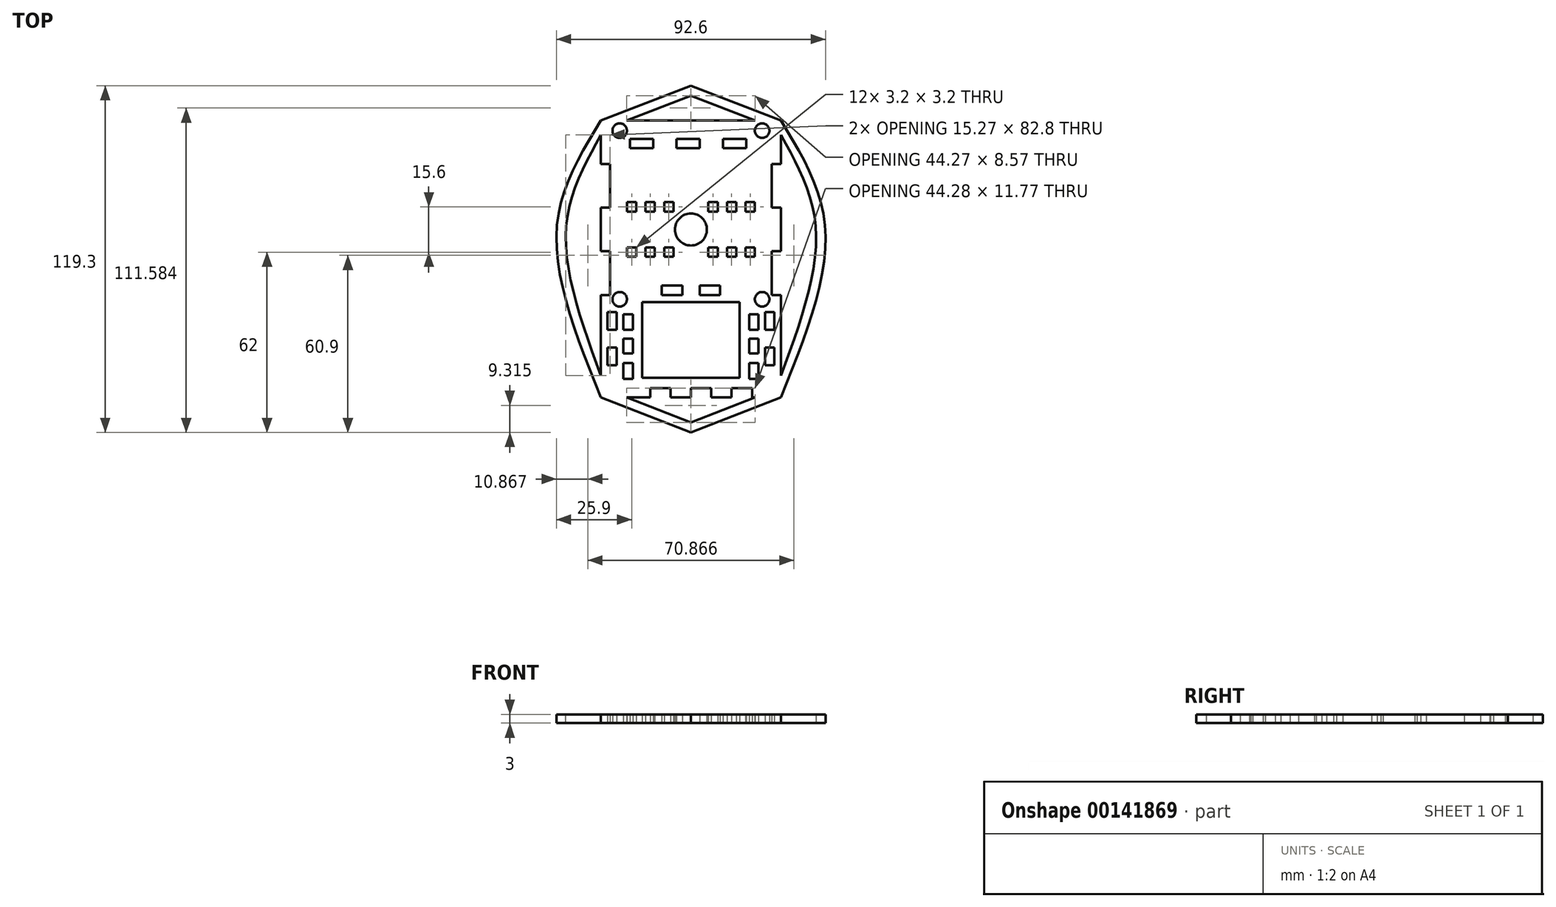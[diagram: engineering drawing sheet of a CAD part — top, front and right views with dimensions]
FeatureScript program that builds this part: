
annotation { "Feature Type Name" : "Feature", "Feature Type Description" : "" }
export const myFeature = defineFeature(function(context is Context, id is Id, definition is map)
    precondition{}
    {
        {
            var Q0;
            Q0=qCreatedBy(makeId("Top.planeOp"),FACE);
            var sketch = newSketch(context, id + "F0", { "sketchPlane" : qUnion([Q0])});
            skLineSegment(sketch, "E0.top", {"start": v(0, 37.5) * mm, "end": v(-22.14, 37.5) * mm});
            skLineSegment(sketch, "E0.right", {"start": v(-31, -32.5) * mm, "end": v(-31, -22.5) * mm});
            skPoint(sketch, "E0.middle", {"position": v(0, 0) * mm});
            skLineSegment(sketch, "E1", {"start": v(-31, 22.5) * mm, "end": v(-27.8, 22.5) * mm});
            skLineSegment(sketch, "E2", {"start": v(-27.8, 22.5) * mm, "end": v(-27.8, 7.5) * mm});
            skLineSegment(sketch, "E3", {"start": v(-27.8, 7.5) * mm, "end": v(-31, 7.5) * mm});
            skLineSegment(sketch, "E4", {"start": v(-31, 7.5) * mm, "end": v(-31, -7.5) * mm});
            skLineSegment(sketch, "E5", {"start": v(-31, -7.5) * mm, "end": v(-27.8, -7.5) * mm});
            skLineSegment(sketch, "E6", {"start": v(-27.8, -7.5) * mm, "end": v(-27.8, -22.5) * mm});
            skLineSegment(sketch, "E7", {"start": v(-27.8, -22.5) * mm, "end": v(-31, -22.5) * mm});
            skLineSegment(sketch, "E8", {"start": v(-31, -22.5) * mm, "end": v(-31, -32.5) * mm});
            skLineSegment(sketch, "E9", {"start": v(27.8, 22.5) * mm, "end": v(31, 22.5) * mm});
            skLineSegment(sketch, "E10", {"start": v(31, 7.5) * mm, "end": v(27.8, 7.5) * mm});
            skLineSegment(sketch, "E11", {"start": v(27.8, -7.5) * mm, "end": v(31, -7.5) * mm});
            skLineSegment(sketch, "E12", {"start": v(31, -22.5) * mm, "end": v(27.8, -22.5) * mm});
            skLineSegment(sketch, "E13.trimOffspring", {"start": v(-31, 22.5) * mm, "end": v(-31, 32.5) * mm});
            skLineSegment(sketch, "E14.trimOffspring", {"start": v(-31, -7.5) * mm, "end": v(-31, 7.5) * mm});
            skCircle(sketch, "E15", {"center": v(0, 0) * mm, "radius": 5.5 * mm});
            skLineSegment(sketch, "E16", {"start": v(0, 0) * mm, "end": v(5.5, 0) * mm, "construction": true});
            skLineSegment(sketch, "E17", {"start": v(-31, 0) * mm, "end": v(0, 0) * mm, "construction": true});
            skLineSegment(sketch, "E18", {"start": v(5.5, 0) * mm, "end": v(6, 0) * mm, "construction": true});
            skLineSegment(sketch, "E19", {"start": v(6, 0) * mm, "end": v(6, 9.4) * mm, "construction": true});
            skLineSegment(sketch, "E20.bottom", {"start": v(6, 9.4) * mm, "end": v(9.2, 9.4) * mm});
            skLineSegment(sketch, "E20.top", {"start": v(6, 6.2) * mm, "end": v(9.2, 6.2) * mm});
            skLineSegment(sketch, "E20.left", {"start": v(6, 9.4) * mm, "end": v(6, 6.2) * mm});
            skLineSegment(sketch, "E20.right", {"start": v(9.2, 9.4) * mm, "end": v(9.2, 6.2) * mm});
            skLineSegment(sketch, "E21", {"start": v(6, 0) * mm, "end": v(12.4, 0) * mm, "construction": true});
            skLineSegment(sketch, "E22", {"start": v(12.4, 0) * mm, "end": v(12.4, 9.4) * mm, "construction": true});
            skLineSegment(sketch, "E23", {"start": v(12.4, 0) * mm, "end": v(18.8, 0) * mm, "construction": true});
            skLineSegment(sketch, "E24", {"start": v(18.8, 0) * mm, "end": v(18.8, 9.4) * mm, "construction": true});
            skLineSegment(sketch, "E25", {"start": v(18.8, 0) * mm, "end": v(24, 0) * mm, "construction": true});
            skLineSegment(sketch, "E26.bottom", {"start": v(12.4, 9.4) * mm, "end": v(15.6, 9.4) * mm});
            skLineSegment(sketch, "E26.top", {"start": v(12.4, 6.2) * mm, "end": v(15.6, 6.2) * mm});
            skLineSegment(sketch, "E26.left", {"start": v(12.4, 9.4) * mm, "end": v(12.4, 6.2) * mm});
            skLineSegment(sketch, "E26.right", {"start": v(15.6, 9.4) * mm, "end": v(15.6, 6.2) * mm});
            skLineSegment(sketch, "E27.bottom", {"start": v(18.8, 9.4) * mm, "end": v(22, 9.4) * mm});
            skLineSegment(sketch, "E27.top", {"start": v(18.8, 6.2) * mm, "end": v(22, 6.2) * mm});
            skLineSegment(sketch, "E27.left", {"start": v(18.8, 9.4) * mm, "end": v(18.8, 6.2) * mm});
            skLineSegment(sketch, "E27.right", {"start": v(22, 9.4) * mm, "end": v(22, 6.2) * mm});
            skLineSegment(sketch, "E28.MirrorCS", {"start": v(-5.5, 0) * mm, "end": v(-6, 0) * mm, "construction": true});
            skLineSegment(sketch, "E29.MirrorCS", {"start": v(-6, 0) * mm, "end": v(-12.4, 0) * mm, "construction": true});
            skLineSegment(sketch, "E30.MirrorCS", {"start": v(-18.8, 0) * mm, "end": v(-24, 0) * mm, "construction": true});
            skLineSegment(sketch, "E31.MirrorCS", {"start": v(-12.4, 0) * mm, "end": v(-18.8, 0) * mm, "construction": true});
            skLineSegment(sketch, "E32", {"start": v(-31, 0) * mm, "end": v(27.8, 0) * mm, "construction": true});
            skLineSegment(sketch, "E33.MirrorCS", {"start": v(0, 0) * mm, "end": v(0, 30) * mm, "construction": true});
            skLineSegment(sketch, "E34.MirrorCS", {"start": v(6, -9.4) * mm, "end": v(9.2, -9.4) * mm});
            skLineSegment(sketch, "E35.MirrorCS", {"start": v(12.4, -9.4) * mm, "end": v(12.4, -6.2) * mm});
            skLineSegment(sketch, "E36.MirrorCS", {"start": v(18.8, -9.4) * mm, "end": v(18.8, -6.2) * mm});
            skLineSegment(sketch, "E37.MirrorCS", {"start": v(6, -9.4) * mm, "end": v(6, -6.2) * mm});
            skLineSegment(sketch, "E38.MirrorCS", {"start": v(18.8, -9.4) * mm, "end": v(22, -9.4) * mm});
            skLineSegment(sketch, "E39.MirrorCS", {"start": v(6, -6.2) * mm, "end": v(9.2, -6.2) * mm});
            skLineSegment(sketch, "E40.MirrorCS", {"start": v(12.4, 0) * mm, "end": v(12.4, -9.4) * mm, "construction": true});
            skLineSegment(sketch, "E41.MirrorCS", {"start": v(9.2, -9.4) * mm, "end": v(9.2, -6.2) * mm});
            skLineSegment(sketch, "E42.MirrorCS", {"start": v(15.6, -9.4) * mm, "end": v(15.6, -6.2) * mm});
            skLineSegment(sketch, "E43.MirrorCS", {"start": v(12.4, -6.2) * mm, "end": v(15.6, -6.2) * mm});
            skLineSegment(sketch, "E44.MirrorCS", {"start": v(12.4, -9.4) * mm, "end": v(15.6, -9.4) * mm});
            skLineSegment(sketch, "E45.MirrorCS", {"start": v(18.8, 0) * mm, "end": v(18.8, -9.4) * mm, "construction": true});
            skLineSegment(sketch, "E46.MirrorCS", {"start": v(18.8, -6.2) * mm, "end": v(22, -6.2) * mm});
            skLineSegment(sketch, "E47.MirrorCS", {"start": v(22, -9.4) * mm, "end": v(22, -6.2) * mm});
            skLineSegment(sketch, "E48.MirrorCS", {"start": v(6, 0) * mm, "end": v(6, -9.4) * mm, "construction": true});
            skLineSegment(sketch, "E49.MirrorCS", {"start": v(-9.2, 9.4) * mm, "end": v(-9.2, 6.2) * mm});
            skLineSegment(sketch, "E50.MirrorCS", {"start": v(-15.6, 9.4) * mm, "end": v(-15.6, 6.2) * mm});
            skLineSegment(sketch, "E51.MirrorCS", {"start": v(-12.4, 9.4) * mm, "end": v(-15.6, 9.4) * mm});
            skLineSegment(sketch, "E52.MirrorCS", {"start": v(-18.8, 6.2) * mm, "end": v(-22, 6.2) * mm});
            skLineSegment(sketch, "E53.MirrorCS", {"start": v(-18.8, 9.4) * mm, "end": v(-18.8, 6.2) * mm});
            skLineSegment(sketch, "E54.MirrorCS", {"start": v(-6, 9.4) * mm, "end": v(-9.2, 9.4) * mm});
            skLineSegment(sketch, "E55.MirrorCS", {"start": v(-22, 9.4) * mm, "end": v(-22, 6.2) * mm});
            skLineSegment(sketch, "E56.MirrorCS", {"start": v(-18.8, 9.4) * mm, "end": v(-22, 9.4) * mm});
            skLineSegment(sketch, "E57.MirrorCS", {"start": v(-6, 6.2) * mm, "end": v(-9.2, 6.2) * mm});
            skLineSegment(sketch, "E58.MirrorCS", {"start": v(-12.4, 9.4) * mm, "end": v(-12.4, 6.2) * mm});
            skLineSegment(sketch, "E59.MirrorCS", {"start": v(-12.4, 6.2) * mm, "end": v(-15.6, 6.2) * mm});
            skLineSegment(sketch, "E60.MirrorCS", {"start": v(-6, 9.4) * mm, "end": v(-6, 6.2) * mm});
            skLineSegment(sketch, "E61.MirrorCS", {"start": v(-18.8, -9.4) * mm, "end": v(-18.8, -6.2) * mm});
            skLineSegment(sketch, "E62.MirrorCS", {"start": v(-12.4, -9.4) * mm, "end": v(-12.4, -6.2) * mm});
            skLineSegment(sketch, "E63.MirrorCS", {"start": v(-6, -9.4) * mm, "end": v(-6, -6.2) * mm});
            skLineSegment(sketch, "E64.MirrorCS", {"start": v(-12.4, -9.4) * mm, "end": v(-15.6, -9.4) * mm});
            skLineSegment(sketch, "E65.MirrorCS", {"start": v(-18.8, -6.2) * mm, "end": v(-22, -6.2) * mm});
            skLineSegment(sketch, "E66.MirrorCS", {"start": v(-18.8, -9.4) * mm, "end": v(-22, -9.4) * mm});
            skLineSegment(sketch, "E67.MirrorCS", {"start": v(-12.4, -6.2) * mm, "end": v(-15.6, -6.2) * mm});
            skLineSegment(sketch, "E68.MirrorCS", {"start": v(-12.4, 0) * mm, "end": v(-12.4, -9.4) * mm, "construction": true});
            skLineSegment(sketch, "E69.MirrorCS", {"start": v(-18.8, 0) * mm, "end": v(-18.8, -9.4) * mm, "construction": true});
            skLineSegment(sketch, "E70.MirrorCS", {"start": v(-6, -9.4) * mm, "end": v(-9.2, -9.4) * mm});
            skLineSegment(sketch, "E71.MirrorCS", {"start": v(-6, 0) * mm, "end": v(-6, -9.4) * mm, "construction": true});
            skLineSegment(sketch, "E72.MirrorCS", {"start": v(-22, -9.4) * mm, "end": v(-22, -6.2) * mm});
            skLineSegment(sketch, "E73.MirrorCS", {"start": v(-9.2, -9.4) * mm, "end": v(-9.2, -6.2) * mm});
            skLineSegment(sketch, "E74.MirrorCS", {"start": v(-6, -6.2) * mm, "end": v(-9.2, -6.2) * mm});
            skLineSegment(sketch, "E75.MirrorCS", {"start": v(-15.6, -9.4) * mm, "end": v(-15.6, -6.2) * mm});
            skLineSegment(sketch, "E76", {"start": v(31, 32.5) * mm, "end": v(31, 22.5) * mm});
            skLineSegment(sketch, "E77", {"start": v(27.8, 22.5) * mm, "end": v(27.8, 7.5) * mm});
            skLineSegment(sketch, "E78", {"start": v(27.8, -7.5) * mm, "end": v(27.8, -22.5) * mm});
            skLineSegment(sketch, "E79.trimOffspring", {"start": v(31, -22.5) * mm, "end": v(31, -32.5) * mm});
            skLineSegment(sketch, "E80", {"start": v(31, 7.5) * mm, "end": v(31, -7.5) * mm});
            skLineSegment(sketch, "E81", {"start": v(31, 22.5) * mm, "end": v(34.2, 22.5) * mm});
            skLineSegment(sketch, "E82", {"start": v(0, 37.5) * mm, "end": v(0, 49.5) * mm, "construction": true});
            skPoint(sketch, "E82.startSnap0", {"position": v(0, 15) * mm});
            skLineSegment(sketch, "E83", {"start": v(0, 43.5) * mm, "end": v(34.2, 43.5) * mm, "construction": true});
            skLineSegment(sketch, "E84", {"start": v(0, 43.5) * mm, "end": v(-40.16, 43.5) * mm, "construction": true});
            skLineSegment(sketch, "E85", {"start": v(34.2, 37.5) * mm, "end": v(34.2, 43.5) * mm, "construction": true});
            skLineSegment(sketch, "E86", {"start": v(-31, 0) * mm, "end": v(-43, 0) * mm, "construction": true});
            skLineSegment(sketch, "E87", {"start": v(-27.8, 15) * mm, "end": v(-54.38, 15) * mm, "construction": true});
            skLineSegment(sketch, "E88", {"start": v(-27.8, -15) * mm, "end": v(-55.02, -15) * mm, "construction": true});
            skLineSegment(sketch, "E89", {"start": v(-31, 0) * mm, "end": v(-31, -20) * mm, "construction": true});
            skLineSegment(sketch, "E90", {"start": v(-31, 0) * mm, "end": v(-31, 20) * mm, "construction": true});
            skLineSegment(sketch, "E91", {"start": v(-31, 20) * mm, "end": v(-43, 20) * mm, "construction": true});
            skLineSegment(sketch, "E92", {"start": v(-43, 20) * mm, "end": v(-43, -20) * mm, "construction": true});
            skLineSegment(sketch, "E93", {"start": v(-31, -32.5) * mm, "end": v(-31, -28.4) * mm, "construction": true});
            skLineSegment(sketch, "E94", {"start": v(-31, 37.5) * mm, "end": v(0, 49.5) * mm});
            skLineSegment(sketch, "E95", {"start": v(0, 49.5) * mm, "end": v(31, 37.5) * mm});
            skLineSegment(sketch, "E96", {"start": v(0, 49.5) * mm, "end": v(0, 46.3) * mm, "construction": true});
            skLineSegment(sketch, "E97", {"start": v(0, 46.07) * mm, "end": v(-22.14, 37.5) * mm, "construction": true});
            skLineSegment(sketch, "E98.MirrorCS", {"start": v(0, 46.07) * mm, "end": v(22.14, 37.5) * mm, "construction": true});
            skLineSegment(sketch, "E99", {"start": v(0, 46.07) * mm, "end": v(22.14, 37.5) * mm});
            skLineSegment(sketch, "E100", {"start": v(0, 46.07) * mm, "end": v(-22.14, 37.5) * mm});
            skPoint(sketch, "E101.orphan", {"position": v(27.8, 37.5) * mm});
            skLineSegment(sketch, "E102", {"start": v(0, 37.5) * mm, "end": v(22.14, 37.5) * mm});
            skPoint(sketch, "E0.left.start.orphan", {"position": v(31, -37.5) * mm});
            skLineSegment(sketch, "E103", {"start": v(-43, 0) * mm, "end": v(-46.2, 0) * mm, "construction": true});
            skLineSegment(sketch, "E104", {"start": v(-31, 37.5) * mm, "end": v(31, 37.5) * mm, "construction": true});
            skLineSegment(sketch, "E105", {"start": v(-31, 34) * mm, "end": v(31, 34) * mm, "construction": true});
            skLineSegment(sketch, "E106", {"start": v(0, 34) * mm, "end": v(-24.5, 34) * mm, "construction": true});
            skLineSegment(sketch, "E107", {"start": v(-24.5, 34) * mm, "end": v(-24.5, -24) * mm, "construction": true});
            skLineSegment(sketch, "E108", {"start": v(24.5, 34) * mm, "end": v(24.5, -24) * mm, "construction": true});
            skLineSegment(sketch, "E109.MirrorCS", {"start": v(-13, 28) * mm, "end": v(-21, 28) * mm});
            skLineSegment(sketch, "E110.MirrorCS", {"start": v(-13, 28) * mm, "end": v(-5, 28) * mm, "construction": true});
            skLineSegment(sketch, "E111.MirrorCS", {"start": v(-5, 28) * mm, "end": v(-5, 31.2) * mm});
            skLineSegment(sketch, "E112.MirrorCS", {"start": v(3, 28) * mm, "end": v(-5, 28) * mm});
            skLineSegment(sketch, "E113.MirrorCS", {"start": v(3, 28) * mm, "end": v(11, 28) * mm, "construction": true});
            skLineSegment(sketch, "E114.MirrorCS", {"start": v(19, 28) * mm, "end": v(11, 28) * mm});
            skLineSegment(sketch, "E115.MirrorCS", {"start": v(-21, 28) * mm, "end": v(-21, 31.2) * mm});
            skLineSegment(sketch, "E116.MirrorCS", {"start": v(-13, 31.2) * mm, "end": v(-13, 28) * mm});
            skLineSegment(sketch, "E117.MirrorCS", {"start": v(-5, 31.2) * mm, "end": v(3, 31.2) * mm});
            skLineSegment(sketch, "E118.MirrorCS", {"start": v(3, 31.2) * mm, "end": v(3, 28) * mm});
            skLineSegment(sketch, "E119.MirrorCS", {"start": v(11, 28) * mm, "end": v(11, 31.2) * mm});
            skLineSegment(sketch, "E120.MirrorCS", {"start": v(19, 31.2) * mm, "end": v(19, 28) * mm});
            skLineSegment(sketch, "E121.MirrorCS", {"start": v(11, 31.2) * mm, "end": v(19, 31.2) * mm});
            skLineSegment(sketch, "E122.MirrorCS", {"start": v(0, 28) * mm, "end": v(21, 28) * mm, "construction": true});
            skLineSegment(sketch, "E123.MirrorCS", {"start": v(0, 28) * mm, "end": v(-21, 28) * mm, "construction": true});
            skLineSegment(sketch, "E124.MirrorCS", {"start": v(-21, 31.2) * mm, "end": v(-13, 31.2) * mm});
            skLineSegment(sketch, "E125.trimOffspring", {"start": v(-31, 32.5) * mm, "end": v(-31, 22.5) * mm});
            skLineSegment(sketch, "E126", {"start": v(43, 0) * mm, "end": v(46.2, 0) * mm, "construction": true});
            skLineSegment(sketch, "E127", {"start": v(0, -23.1) * mm, "end": v(-21.89, -23.1) * mm, "construction": true});
            skLineSegment(sketch, "E128", {"start": v(0, -23.1) * mm, "end": v(22.57, -23.1) * mm, "construction": true});
            skCircle(sketch, "E129", {"center": v(24.5, -24) * mm, "radius": 2.5 * mm});
            skCircle(sketch, "E130", {"center": v(-24.5, -24) * mm, "radius": 2.5 * mm});
            skCircle(sketch, "E131", {"center": v(-24.5, 34) * mm, "radius": 2.5 * mm});
            skCircle(sketch, "E132", {"center": v(24.5, 34) * mm, "radius": 2.5 * mm});
            skLineSegment(sketch, "E133", {"start": v(-31, -28.4) * mm, "end": v(31, -28.4) * mm, "construction": true});
            skLineSegment(sketch, "E134", {"start": v(0, -28.4) * mm, "end": v(0, -57.8) * mm, "construction": true});
            skLineSegment(sketch, "E135", {"start": v(0, -28.4) * mm, "end": v(-25, -28.4) * mm, "construction": true});
            skLineSegment(sketch, "E136", {"start": v(-25, -28.4) * mm, "end": v(-25, -57.8) * mm, "construction": true});
            skLineSegment(sketch, "E137", {"start": v(0, -28.4) * mm, "end": v(25, -28.4) * mm, "construction": true});
            skLineSegment(sketch, "E138", {"start": v(25, -28.4) * mm, "end": v(25, -57.8) * mm, "construction": true});
            skLineSegment(sketch, "E139", {"start": v(22.14, -57.8) * mm, "end": v(21, -57.8) * mm, "construction": true});
            skLineSegment(sketch, "E140", {"start": v(25, -28.4) * mm, "end": v(20, -28.4) * mm, "construction": true});
            skLineSegment(sketch, "E141.MirrorCS", {"start": v(-20, -28.4) * mm, "end": v(-20, -29.13) * mm, "construction": true});
            skLineSegment(sketch, "E142.MirrorCS", {"start": v(-20, -33.33) * mm, "end": v(-20, -29.13) * mm});
            skLineSegment(sketch, "E143.MirrorCS", {"start": v(-23.2, -29.13) * mm, "end": v(-23.2, -33.33) * mm});
            skLineSegment(sketch, "E144.MirrorCS", {"start": v(-20, -29.13) * mm, "end": v(-23.2, -29.13) * mm});
            skLineSegment(sketch, "E145.MirrorCS", {"start": v(-20, -50.13) * mm, "end": v(-20, -45.93) * mm});
            skLineSegment(sketch, "E146.MirrorCS", {"start": v(-23.2, -45.93) * mm, "end": v(-23.2, -50.13) * mm});
            skLineSegment(sketch, "E147.MirrorCS", {"start": v(-20, -45.93) * mm, "end": v(-23.2, -45.93) * mm});
            skLineSegment(sketch, "E148.MirrorCS", {"start": v(-20, -41.73) * mm, "end": v(-20, -45.93) * mm, "construction": true});
            skLineSegment(sketch, "E149.MirrorCS", {"start": v(-20, -41.73) * mm, "end": v(-20, -37.53) * mm});
            skLineSegment(sketch, "E150.MirrorCS", {"start": v(-23.2, -37.53) * mm, "end": v(-23.2, -41.73) * mm});
            skLineSegment(sketch, "E151.MirrorCS", {"start": v(-20, -37.53) * mm, "end": v(-23.2, -37.53) * mm});
            skLineSegment(sketch, "E152.MirrorCS", {"start": v(-20, -33.33) * mm, "end": v(-20, -37.53) * mm, "construction": true});
            skLineSegment(sketch, "E153", {"start": v(-22.14, -57.8) * mm, "end": v(-14, -57.8) * mm});
            skLineSegment(sketch, "E154", {"start": v(0, -57.8) * mm, "end": v(0, -69.8) * mm, "construction": true});
            skLineSegment(sketch, "E155", {"start": v(0, -69.8) * mm, "end": v(0, -66.37) * mm, "construction": true});
            skLineSegment(sketch, "E156", {"start": v(-22.14, -57.8) * mm, "end": v(0, -66.37) * mm});
            skLineSegment(sketch, "E157", {"start": v(0, -66.37) * mm, "end": v(22.14, -57.8) * mm});
            skLineSegment(sketch, "E158", {"start": v(-31, -57.8) * mm, "end": v(0, -69.8) * mm});
            skLineSegment(sketch, "E159", {"start": v(0, -69.8) * mm, "end": v(31, -57.8) * mm});
            skLineSegment(sketch, "E160", {"start": v(-31, -52.8) * mm, "end": v(31, -52.8) * mm, "construction": true});
            skFitSpline(sketch, "E161", {"points": [v(31, 37.5) * mm, v(46.2, 0) * mm, v(31, -57.8) * mm], "startDerivative": vector(47.53, -78.05) * mm, "endDerivative": vector(-44.54, -111.47) * mm});
            skLineSegment(sketch, "E162", {"start": v(0, -23.1) * mm, "end": v(0, -52.8) * mm, "construction": true});
            skLineSegment(sketch, "E163.bottom", {"start": v(16.8, -24.92) * mm, "end": v(-16.8, -24.92) * mm});
            skLineSegment(sketch, "E163.top", {"start": v(16.8, -50.98) * mm, "end": v(-16.8, -50.98) * mm});
            skLineSegment(sketch, "E163.left", {"start": v(16.8, -24.92) * mm, "end": v(16.8, -50.98) * mm});
            skLineSegment(sketch, "E163.right", {"start": v(-16.8, -24.92) * mm, "end": v(-16.8, -50.98) * mm});
            skPoint(sketch, "E163.middle", {"position": v(0, -37.95) * mm});
            skLineSegment(sketch, "E164", {"start": v(-22.14, -57.8) * mm, "end": v(-14, -57.8) * mm, "construction": true});
            skLineSegment(sketch, "E165", {"start": v(-7, -57.8) * mm, "end": v(0, -57.8) * mm, "construction": true});
            skLineSegment(sketch, "E166", {"start": v(7, -57.8) * mm, "end": v(14, -57.8) * mm, "construction": true});
            skLineSegment(sketch, "E167", {"start": v(-14, -57.8) * mm, "end": v(-14, -54.6) * mm});
            skLineSegment(sketch, "E168", {"start": v(-14, -54.6) * mm, "end": v(-7, -54.6) * mm});
            skLineSegment(sketch, "E169", {"start": v(-7, -54.6) * mm, "end": v(-7, -57.8) * mm});
            skLineSegment(sketch, "E170", {"start": v(0, -57.8) * mm, "end": v(0, -54.6) * mm});
            skLineSegment(sketch, "E171", {"start": v(0, -54.6) * mm, "end": v(7, -54.6) * mm});
            skLineSegment(sketch, "E172", {"start": v(7, -54.6) * mm, "end": v(7, -57.8) * mm});
            skLineSegment(sketch, "E173", {"start": v(14, -57.8) * mm, "end": v(14, -54.6) * mm});
            skLineSegment(sketch, "E174", {"start": v(14, -54.6) * mm, "end": v(21, -54.6) * mm});
            skLineSegment(sketch, "E175", {"start": v(21, -54.6) * mm, "end": v(21, -57.8) * mm});
            skLineSegment(sketch, "E176.trimOffspring", {"start": v(-14, -57.8) * mm, "end": v(-22.14, -57.8) * mm, "construction": true});
            skLineSegment(sketch, "E177.trimOffspring", {"start": v(-7, -57.8) * mm, "end": v(0, -57.8) * mm});
            skLineSegment(sketch, "E178.trimOffspring", {"start": v(14, -57.8) * mm, "end": v(7, -57.8) * mm, "construction": true});
            skLineSegment(sketch, "E179.trimOffspring", {"start": v(21, -57.8) * mm, "end": v(22.14, -57.8) * mm});
            skLineSegment(sketch, "E180.trimOffspring", {"start": v(0, -57.8) * mm, "end": v(-7, -57.8) * mm, "construction": true});
            skLineSegment(sketch, "E181.trimOffspring", {"start": v(7, -57.8) * mm, "end": v(14, -57.8) * mm});
            skLineSegment(sketch, "E182", {"start": v(-23.2, -28.4) * mm, "end": v(-23.2, -52.8) * mm, "construction": true});
            skLineSegment(sketch, "E183", {"start": v(-23.2, -28.4) * mm, "end": v(-25.5, -28.4) * mm, "construction": true});
            skLineSegment(sketch, "E184", {"start": v(-25.5, -28.4) * mm, "end": v(-25.5, -52.8) * mm, "construction": true});
            skLineSegment(sketch, "E185", {"start": v(-31, -28.4) * mm, "end": v(-28.7, -28.4) * mm, "construction": true});
            skLineSegment(sketch, "E186", {"start": v(-28.7, -28.4) * mm, "end": v(-28.7, -52.8) * mm, "construction": true});
            skLineSegment(sketch, "E187", {"start": v(-28.7, -28.4) * mm, "end": v(-28.7, -34.5) * mm, "construction": true});
            skLineSegment(sketch, "E188", {"start": v(-28.7, -34.5) * mm, "end": v(-28.7, -40.6) * mm, "construction": true});
            skLineSegment(sketch, "E189", {"start": v(-28.7, -40.6) * mm, "end": v(-28.7, -46.7) * mm, "construction": true});
            skLineSegment(sketch, "E190.bottom", {"start": v(-28.7, -28.4) * mm, "end": v(-25.5, -28.4) * mm});
            skLineSegment(sketch, "E190.top", {"start": v(-28.7, -34.5) * mm, "end": v(-25.5, -34.5) * mm});
            skLineSegment(sketch, "E190.left", {"start": v(-28.7, -28.4) * mm, "end": v(-28.7, -34.5) * mm});
            skLineSegment(sketch, "E190.right", {"start": v(-25.5, -28.4) * mm, "end": v(-25.5, -34.5) * mm});
            skLineSegment(sketch, "E191.bottom", {"start": v(-28.7, -40.6) * mm, "end": v(-25.5, -40.6) * mm});
            skLineSegment(sketch, "E191.top", {"start": v(-28.7, -46.7) * mm, "end": v(-25.5, -46.7) * mm});
            skLineSegment(sketch, "E191.left", {"start": v(-28.7, -40.6) * mm, "end": v(-28.7, -46.7) * mm});
            skLineSegment(sketch, "E191.right", {"start": v(-25.5, -40.6) * mm, "end": v(-25.5, -46.7) * mm});
            skLineSegment(sketch, "E192.MirrorCS", {"start": v(28.7, -28.4) * mm, "end": v(28.7, -34.5) * mm});
            skLineSegment(sketch, "E193.MirrorCS", {"start": v(28.7, -40.6) * mm, "end": v(28.7, -46.7) * mm});
            skLineSegment(sketch, "E194.MirrorCS", {"start": v(25.5, -28.4) * mm, "end": v(25.5, -34.5) * mm});
            skLineSegment(sketch, "E195.MirrorCS", {"start": v(28.7, -34.5) * mm, "end": v(25.5, -34.5) * mm});
            skLineSegment(sketch, "E196.MirrorCS", {"start": v(28.7, -28.4) * mm, "end": v(25.5, -28.4) * mm});
            skLineSegment(sketch, "E197.MirrorCS", {"start": v(28.7, -40.6) * mm, "end": v(28.7, -46.7) * mm, "construction": true});
            skLineSegment(sketch, "E198.MirrorCS", {"start": v(28.7, -34.5) * mm, "end": v(28.7, -40.6) * mm, "construction": true});
            skLineSegment(sketch, "E199.MirrorCS", {"start": v(28.7, -28.4) * mm, "end": v(28.7, -34.5) * mm, "construction": true});
            skLineSegment(sketch, "E200.MirrorCS", {"start": v(25.5, -40.6) * mm, "end": v(25.5, -46.7) * mm});
            skLineSegment(sketch, "E201.MirrorCS", {"start": v(28.7, -46.7) * mm, "end": v(25.5, -46.7) * mm});
            skLineSegment(sketch, "E202.MirrorCS", {"start": v(28.7, -40.6) * mm, "end": v(25.5, -40.6) * mm});
            skLineSegment(sketch, "E203.bottom", {"start": v(-23.2, -45.93) * mm, "end": v(-20, -45.93) * mm});
            skLineSegment(sketch, "E203.top", {"start": v(-23.2, -51.43) * mm, "end": v(-20, -51.43) * mm});
            skLineSegment(sketch, "E203.left", {"start": v(-23.2, -45.93) * mm, "end": v(-23.2, -51.43) * mm});
            skLineSegment(sketch, "E203.right", {"start": v(-20, -45.93) * mm, "end": v(-20, -51.43) * mm});
            skLineSegment(sketch, "E204.bottom", {"start": v(-23.2, -37.53) * mm, "end": v(-20, -37.53) * mm});
            skLineSegment(sketch, "E204.top", {"start": v(-23.2, -42.57) * mm, "end": v(-20, -42.57) * mm});
            skLineSegment(sketch, "E204.left", {"start": v(-23.2, -37.53) * mm, "end": v(-23.2, -42.57) * mm});
            skLineSegment(sketch, "E204.right", {"start": v(-20, -37.53) * mm, "end": v(-20, -42.57) * mm});
            skLineSegment(sketch, "E205.bottom", {"start": v(-23.2, -29.13) * mm, "end": v(-20, -29.13) * mm});
            skLineSegment(sketch, "E205.top", {"start": v(-23.2, -34.55) * mm, "end": v(-20, -34.55) * mm});
            skLineSegment(sketch, "E205.left", {"start": v(-23.2, -29.13) * mm, "end": v(-23.2, -34.55) * mm});
            skLineSegment(sketch, "E205.right", {"start": v(-20, -29.13) * mm, "end": v(-20, -34.55) * mm});
            skLineSegment(sketch, "E206.MirrorCS", {"start": v(23.2, -29.13) * mm, "end": v(20, -29.13) * mm});
            skLineSegment(sketch, "E207.MirrorCS", {"start": v(23.2, -37.53) * mm, "end": v(23.2, -42.57) * mm});
            skLineSegment(sketch, "E208.MirrorCS", {"start": v(23.2, -29.13) * mm, "end": v(23.2, -33.33) * mm});
            skLineSegment(sketch, "E209.MirrorCS", {"start": v(20, -33.33) * mm, "end": v(20, -29.13) * mm});
            skLineSegment(sketch, "E210.MirrorCS", {"start": v(20, -45.93) * mm, "end": v(20, -51.43) * mm});
            skLineSegment(sketch, "E211.MirrorCS", {"start": v(23.2, -45.93) * mm, "end": v(23.2, -51.43) * mm});
            skLineSegment(sketch, "E212.MirrorCS", {"start": v(23.2, -45.93) * mm, "end": v(20, -45.93) * mm});
            skLineSegment(sketch, "E213.MirrorCS", {"start": v(20, -37.53) * mm, "end": v(23.2, -37.53) * mm});
            skLineSegment(sketch, "E214.MirrorCS", {"start": v(20, -37.53) * mm, "end": v(20, -42.57) * mm});
            skLineSegment(sketch, "E215.MirrorCS", {"start": v(20, -29.13) * mm, "end": v(20, -34.55) * mm});
            skLineSegment(sketch, "E216.MirrorCS", {"start": v(20, -41.73) * mm, "end": v(20, -45.93) * mm, "construction": true});
            skLineSegment(sketch, "E217.MirrorCS", {"start": v(23.2, -29.13) * mm, "end": v(23.2, -34.55) * mm});
            skLineSegment(sketch, "E218.MirrorCS", {"start": v(20, -45.93) * mm, "end": v(23.2, -45.93) * mm});
            skLineSegment(sketch, "E219.MirrorCS", {"start": v(23.2, -34.55) * mm, "end": v(20, -34.55) * mm});
            skLineSegment(sketch, "E220.MirrorCS", {"start": v(20, -50.13) * mm, "end": v(20, -45.93) * mm});
            skLineSegment(sketch, "E221.MirrorCS", {"start": v(23.2, -42.57) * mm, "end": v(20, -42.57) * mm});
            skLineSegment(sketch, "E222.MirrorCS", {"start": v(23.2, -37.53) * mm, "end": v(20, -37.53) * mm});
            skLineSegment(sketch, "E223.MirrorCS", {"start": v(23.2, -51.43) * mm, "end": v(20, -51.43) * mm});
            skLineSegment(sketch, "E224.MirrorCS", {"start": v(20, -33.33) * mm, "end": v(20, -37.53) * mm, "construction": true});
            skLineSegment(sketch, "E225.MirrorCS", {"start": v(23.2, -37.53) * mm, "end": v(23.2, -41.73) * mm});
            skLineSegment(sketch, "E226.MirrorCS", {"start": v(20, -41.73) * mm, "end": v(20, -37.53) * mm});
            skLineSegment(sketch, "E227.MirrorCS", {"start": v(23.2, -45.93) * mm, "end": v(23.2, -50.13) * mm});
            skLineSegment(sketch, "E228.MirrorCS", {"start": v(20, -29.13) * mm, "end": v(23.2, -29.13) * mm});
            skLineSegment(sketch, "E229", {"start": v(-27.8, -15) * mm, "end": v(-15, -15) * mm, "construction": true});
            skLineSegment(sketch, "E230", {"start": v(0, 0) * mm, "end": v(0, -23.1) * mm, "construction": true});
            skLineSegment(sketch, "E231", {"start": v(3, -15) * mm, "end": v(15, -15) * mm, "construction": true});
            skLineSegment(sketch, "E232.trimOffspring", {"start": v(3, -15) * mm, "end": v(27.8, -15) * mm, "construction": true});
            skLineSegment(sketch, "E233", {"start": v(-27.8, -22.5) * mm, "end": v(-27.8, -15) * mm, "construction": true});
            skLineSegment(sketch, "E234.MirrorCS", {"start": v(-3, -22.5) * mm, "end": v(-10, -22.5) * mm});
            skLineSegment(sketch, "E235.MirrorCS", {"start": v(-10, -22.5) * mm, "end": v(-10, -19.3) * mm});
            skLineSegment(sketch, "E236.MirrorCS", {"start": v(-3, -22.5) * mm, "end": v(-10, -22.5) * mm, "construction": true});
            skLineSegment(sketch, "E237.MirrorCS", {"start": v(-3, -19.3) * mm, "end": v(-3, -22.5) * mm});
            skLineSegment(sketch, "E238.MirrorCS", {"start": v(-10, -19.3) * mm, "end": v(-3, -19.3) * mm});
            skLineSegment(sketch, "E239.MirrorCS", {"start": v(3, -22.5) * mm, "end": v(3, -19.3) * mm});
            skLineSegment(sketch, "E240.MirrorCS", {"start": v(3, -19.3) * mm, "end": v(10, -19.3) * mm});
            skLineSegment(sketch, "E241.MirrorCS", {"start": v(10, -19.3) * mm, "end": v(10, -22.5) * mm});
            skLineSegment(sketch, "E242.MirrorCS", {"start": v(3, -22.5) * mm, "end": v(10, -22.5) * mm});
            skLineSegment(sketch, "E243", {"start": v(0, -19.3) * mm, "end": v(-24.5, -19.3) * mm, "construction": true});
            skLineSegment(sketch, "E244", {"start": v(-31, 37.5) * mm, "end": v(-66.4, 37.5) * mm, "construction": true});
            skLineSegment(sketch, "E245", {"start": v(-66.4, 37.5) * mm, "end": v(-66.4, -57.8) * mm, "construction": true});
            skLineSegment(sketch, "E246", {"start": v(-66.4, -57.8) * mm, "end": v(-31, -57.8) * mm, "construction": true});
            skLineSegment(sketch, "E247", {"start": v(-66.4, -10.15) * mm, "end": v(-46.2, -10.15) * mm, "construction": true});
            skLineSegment(sketch, "E248", {"start": v(-46.2, -10.15) * mm, "end": v(-43, -10.15) * mm, "construction": true});
            skLineSegment(sketch, "E249", {"start": v(-31, -50.3) * mm, "end": v(25, -50.3) * mm, "construction": true});
            skLineSegment(sketch, "E250", {"start": v(25, -50.3) * mm, "end": v(31, -50.3) * mm, "construction": true});
            skLineSegment(sketch, "E251", {"start": v(-31, 34.3) * mm, "end": v(-31, 34) * mm, "construction": true});
            skFitSpline(sketch, "E252", {"points": [v(31, 32.5) * mm, v(43, 0) * mm, v(31, -50.3) * mm], "startDerivative": vector(37.57, -67.87) * mm, "endDerivative": vector(-35.15, -96.77) * mm});
            skFitSpline(sketch, "E253.MirrorCS", {"points": [v(-31, 32.5) * mm, v(-43, 0) * mm, v(-31, -50.3) * mm], "startDerivative": vector(-37.57, -67.87) * mm, "endDerivative": vector(35.15, -96.77) * mm});
            skFitSpline(sketch, "E254.MirrorCS", {"points": [v(-31, 37.5) * mm, v(-46.2, 0) * mm, v(-31, -57.8) * mm], "startDerivative": vector(-47.53, -78.05) * mm, "endDerivative": vector(44.54, -111.47) * mm});
            skLineSegment(sketch, "E255.trimOffspring", {"start": v(-31, 32.5) * mm, "end": v(-31, 30) * mm, "construction": true});
            skLineSegment(sketch, "E256", {"start": v(-31, -50.3) * mm, "end": v(-31, -32.5) * mm});
            skLineSegment(sketch, "E257", {"start": v(31, -32.5) * mm, "end": v(31, -50.3) * mm});
            skSolve(sketch);
        }
        {
            var Q0;
            Q0=qSketchRegion(id+"F0",true);
            extrude(context, id + "F1", {"entities" : qUnion([Q0]), "endBound" : BoundingType.SYMMETRIC, "depth" : 3 * mm});
        }
    });
